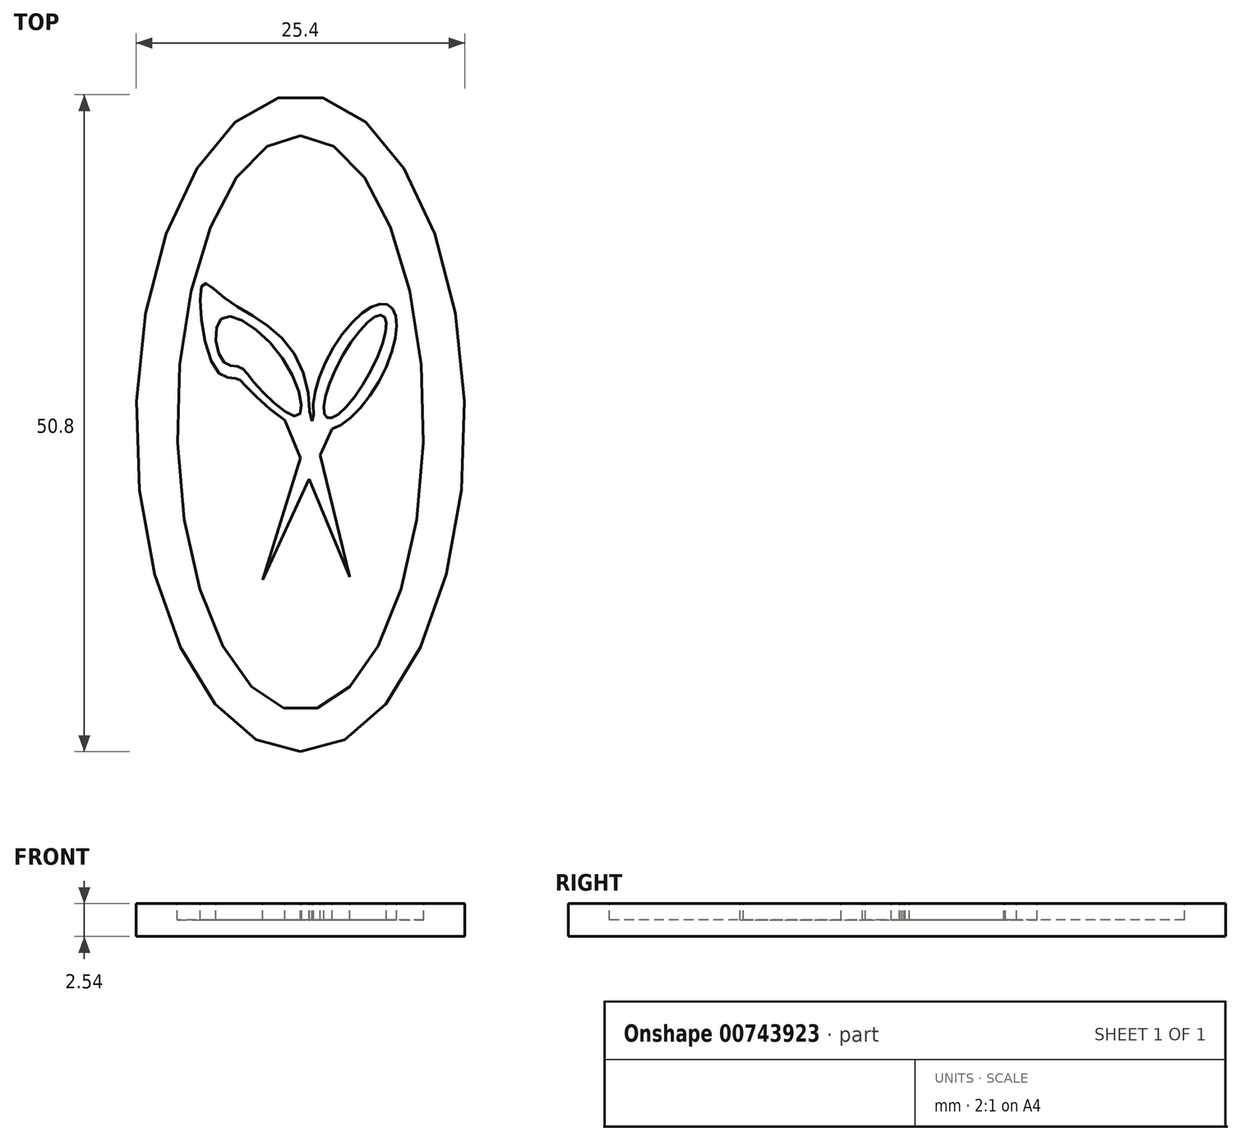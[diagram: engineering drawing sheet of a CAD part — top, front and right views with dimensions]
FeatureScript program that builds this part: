
annotation { "Feature Type Name" : "Feature", "Feature Type Description" : "" }
export const myFeature = defineFeature(function(context is Context, id is Id, definition is map)
    precondition{}
    {
        {
            var Q0;
            Q0=qCreatedBy(makeId("Top.planeOp"),FACE);
            var sketch = newSketch(context, id + "F0", { "sketchPlane" : qUnion([Q0])});
            skEllipse(sketch, "E0", {"center": v(0, 0) * mm, "majorRadius": 25.4 * mm, "minorRadius": 12.7 * mm, "majorAxis": v(0, -1)});
            skSolve(sketch);
        }
        {
            var Q0;
            Q0=qSketchRegion(id+"F0",true);
            extrude(context, id + "F1", {"entities" : qUnion([Q0]), "depth" : 2.54 * mm, "offsetDistance" : 25.4 * mm});
        }
        {
            var Q0;
            Q0=makeQuery(id+"F1.opExtrude","CAP_FACE",FACE,{"disambiguationData":[OSD([sQuery(id+"F0.wireOp",EDGE,"E0")])],"isStart":false});
            var sketch = newSketch(context, id + "F2", { "sketchPlane" : qUnion([Q0])});
            skEllipse(sketch, "E1", {"center": v(0, 0) * mm, "majorRadius": 22.23 * mm, "minorRadius": 9.53 * mm, "majorAxis": v(0, 1)});
            skSolve(sketch);
        }
        {
            var Q0;
            Q0 = qSketchRegion(id + "F2", true);
            extrude(context, id + "F3", {"entities" : qUnion([Q0]), "operationType" : NewBodyOperationType.REMOVE, "oppositeDirection" : true, "depth" : 1.27 * mm, "offsetDistance" : 25.4 * mm});
        }
        {
            var Q0;
            Q0=makeQuery(id+"F2.imprint","IMPRINT",FACE,{"disambiguationData":[TD([[makeQuery(id+"F2.imprint","IMPRINT",EDGE,{"derivedFrom":sQuery(id+"F2.wireOp",EDGE,"E1")}),1.0]])]});
            var sketch = newSketch(context, id + "F4", { "sketchPlane" : qUnion([Q0])});
            skFitSpline(sketch, "E2", {"points": [v(-6.13, 8.09) * mm, v(-1.29, 4.87) * mm, v(-0.24, 0.55) * mm, v(-3.6, 3.16) * mm, v(-4.7, 4.35) * mm, v(-5.99, 4.78) * mm, v(-6.13, 8.09) * mm]});
            skFitSpline(sketch, "E3", {"points": [v(-7.57, 10.73) * mm, v(-6.5, 4.1) * mm, v(-4.98, 3.48) * mm, v(-4.19, 2.85) * mm, v(0.1, -0.15) * mm, v(-0.53, 5.47) * mm, v(-5.97, 9.75) * mm, v(-7.57, 10.73) * mm]});
            skLineSegment(sketch, "E4", {"start": v(-1.2, 0.24) * mm, "end": v(3.81, -11.89) * mm});
            skLineSegment(sketch, "E5", {"start": v(3.81, -11.89) * mm, "end": v(0.69, 0.95) * mm});
            skEllipse(sketch, "E6", {"center": v(4.21, 4.37) * mm, "majorRadius": 5.42 * mm, "minorRadius": 2.17 * mm, "majorAxis": v(-0.48, -0.88)});
            skEllipse(sketch, "E7", {"center": v(4.21, 4.37) * mm, "majorRadius": 4.5 * mm, "minorRadius": 1.24 * mm, "majorAxis": v(-0.48, -0.88)});
            skLineSegment(sketch, "E8", {"start": v(-2.92, -12.13) * mm, "end": v(2.44, -0.44) * mm});
            skLineSegment(sketch, "E9", {"start": v(-2.92, -12.13) * mm, "end": v(1.01, 0.63) * mm});
            skLineSegment(sketch, "E10.0", {"start": v(-6.94, 8.53) * mm, "end": v(-6.2, 14.16) * mm, "construction": true});
            skSolve(sketch);
        }
        {
            var Q0;
            Q0 = qSketchRegion(id + "F4", true);
            extrude(context, id + "F5", {"entities" : qUnion([Q0]), "operationType" : NewBodyOperationType.ADD, "oppositeDirection" : true, "depth" : 1.52 * mm, "offsetDistance" : 25.4 * mm});
        }
    });
